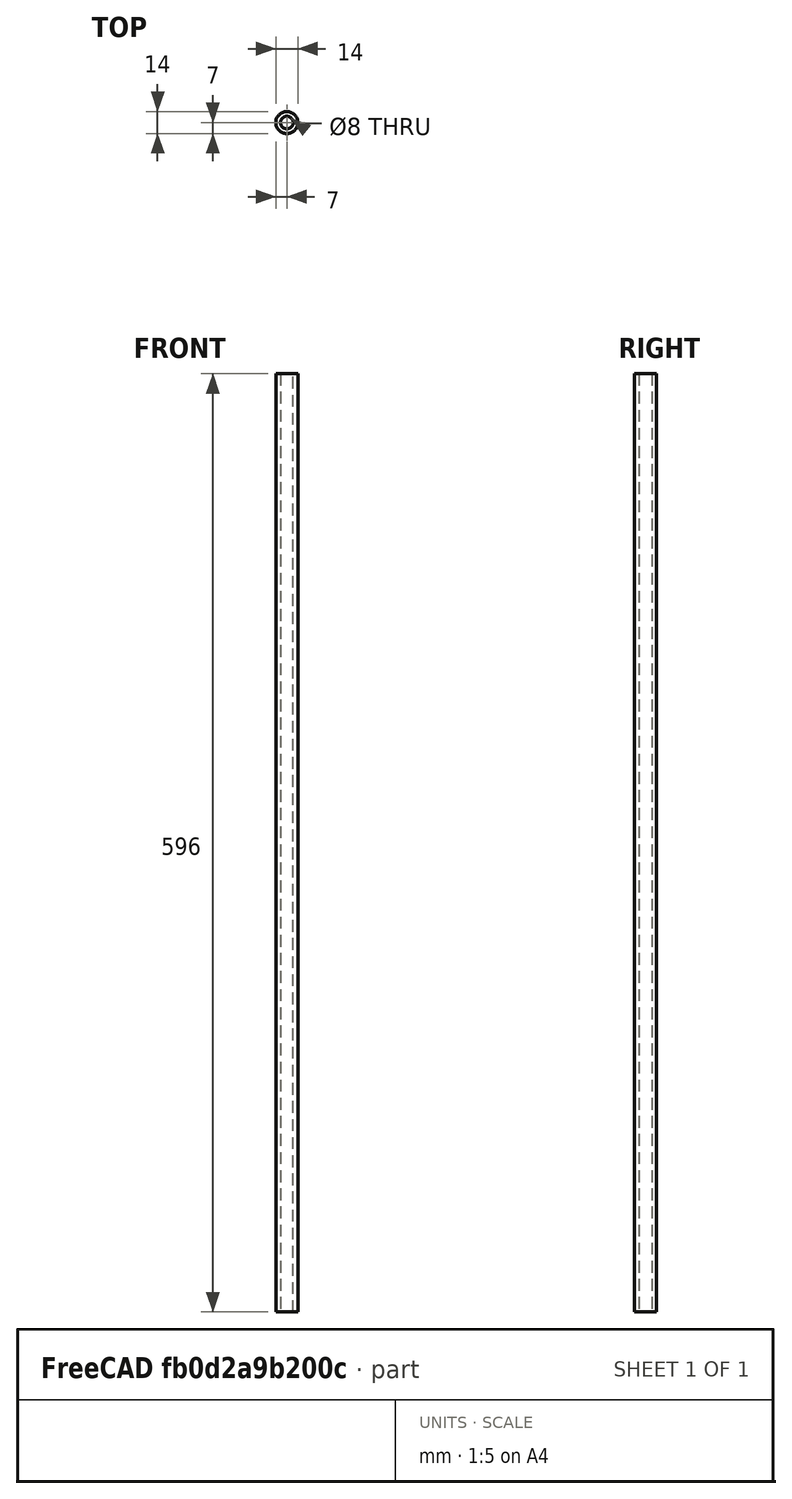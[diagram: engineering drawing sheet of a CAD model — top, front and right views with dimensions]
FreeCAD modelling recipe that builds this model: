
FCSTD DOCUMENT  (FreeCAD 1.0R39319 (Git))
Label: pcp_barel_14x3x596mm_8mmid
License: All rights reserved
LicenseURL: https://en.wikipedia.org/wiki/All_rights_reserved
objects: Sketcher::SketchObject×1, PartDesign::Pad×1, PartDesign::Body×1
note: 6 computed .brp shape members not serialized (recipe doc carries the construction recipe); baked Part::Feature solids carry a one-line shape summary decoded from their .brp

FEATURE [Sketcher::SketchObject] Sketch
  ArcFitTolerance = 1e-06
  AttachmentSupport = -> [XY_Plane]
  FullyConstrained = true
  MakeInternals = false
  MapMode = 5
  sketch-geometry (2):
    g0: Circle CenterX=0 CenterY=0 CenterZ=0 NormalX=0 NormalY=0 NormalZ=1 AngleXU=0 Radius=7
    g1: Circle CenterX=0 CenterY=0 CenterZ=0 NormalX=0 NormalY=0 NormalZ=1 AngleXU=0 Radius=4
  constraints (4):
    c: Diameter(g0) = 14
    c: Coincident(g0,g-1)
    c: Diameter(g1) = 8
    c: Coincident(g1,g0)
FEATURE [PartDesign::Pad] Pad
  Direction = (0,0,1)
  Length = 596
  Length2 = 10
  Profile = -> Sketch
  ReferenceAxis = -> Sketch [N_Axis]
  Refine = true
  Suppressed = false
  Type = 0
FEATURE [PartDesign::Body] Body
  AllowCompound = false
  Group = -> [Sketch,Pad]
  Origin = -> Origin
  Tip = -> Pad
